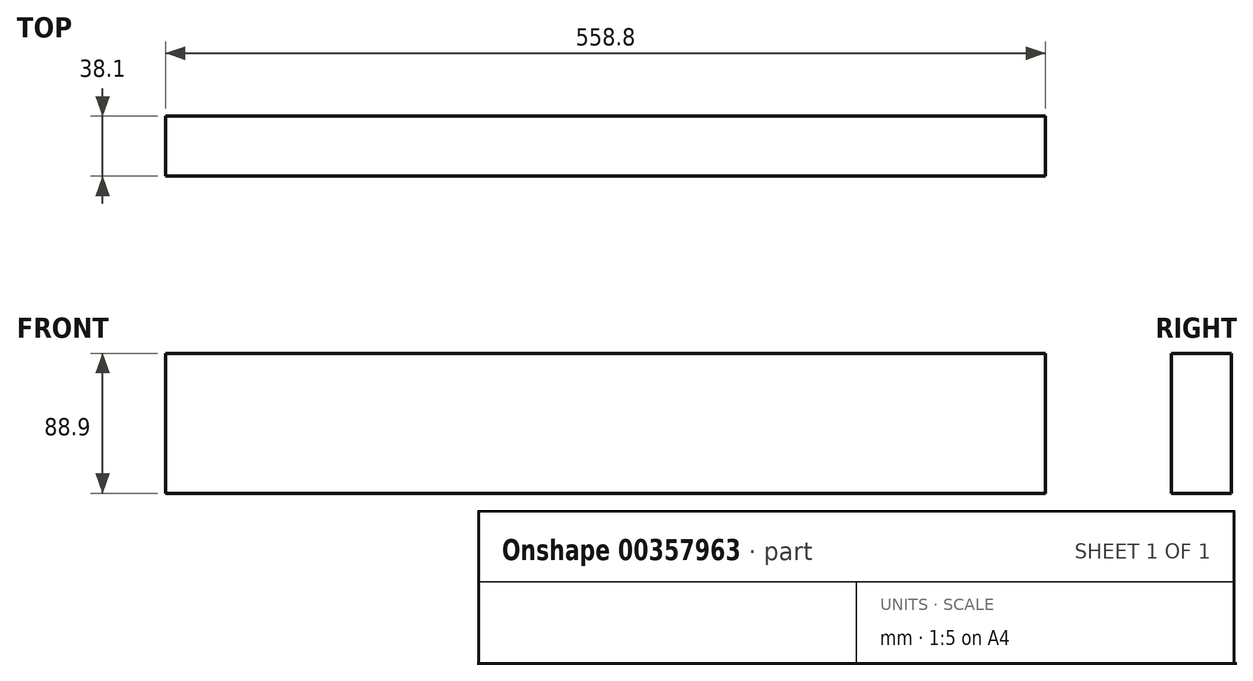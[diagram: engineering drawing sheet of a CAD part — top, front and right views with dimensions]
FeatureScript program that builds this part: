
annotation { "Feature Type Name" : "Feature", "Feature Type Description" : "" }
export const myFeature = defineFeature(function(context is Context, id is Id, definition is map)
    precondition{}
    {
        {
            var Q0;
            Q0=qCreatedBy(makeId("Right.planeOp"),FACE);
            var sketch = newSketch(context, id + "F0", { "sketchPlane" : qUnion([Q0])});
            skLineSegment(sketch, "E0.bottom", {"start": v(19.05, -46.65) * mm, "end": v(-19.05, -46.65) * mm});
            skLineSegment(sketch, "E0.top", {"start": v(19.05, 42.25) * mm, "end": v(-19.05, 42.25) * mm});
            skLineSegment(sketch, "E0.left", {"start": v(19.05, -46.65) * mm, "end": v(19.05, 42.25) * mm});
            skLineSegment(sketch, "E0.right", {"start": v(-19.05, -46.65) * mm, "end": v(-19.05, 42.25) * mm});
            skPoint(sketch, "E0.middle", {"position": v(0, -2.2) * mm});
            skSolve(sketch);
        }
        {
            var Q0;
            Q0 = qSketchRegion(id + "F0", true);
            extrude(context, id + "F1", {"entities" : qUnion([Q0]), "depth" : 558.8 * mm, "symmetric" : true});
        }
    });
